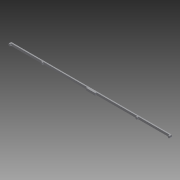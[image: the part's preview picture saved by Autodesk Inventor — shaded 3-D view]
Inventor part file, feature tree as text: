
AUTODESK INVENTOR PART (.ipt)
format: ipt  version: 2011 (Build 150239000, 239)  size: 106,496 bytes
history: native  units: in
note: dims shown in document units (in); Inventor stores cm internally (conversion verified against a paired STEP export)
features: extrude x5, sketch x5
ambient origin geometry x8: Origin, YZ Plane, XZ Plane, XY Plane, X Axis, Y Axis, Z Axis, Center Point
bodies: Solid1 (feature_tree)
feature tree (10):
  extrude  "Extrusion1"  Depth=0.25in
  extrude  "Extrusion2"  Depth=0.125in
  extrude  "Extrusion3"  Depth=3.531in
  extrude  "Extrusion4"  Depth=0.125in TaperAngle=0.0deg
  extrude  "Extrusion5"  Depth=0.5in
  sketch  "Sketch1"  dims[d0=17.469in d1=0.25in]
  sketch  "Sketch2"  dims[d2=0.125in d3=0.0in d4=0.125in]
  sketch  "Sketch3"  dims[d5=3.531in d6=3.531in]
  sketch  "Sketch4"  dims[d7=0.125in d8=0.0in d9=0.125in d10=0.0in]
  sketch  "Sketch5"  dims[d11=0.125in d12=0.0in d13=0.5in d14=1.0in d15=0.125in d16=0.0in]
